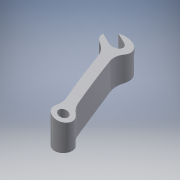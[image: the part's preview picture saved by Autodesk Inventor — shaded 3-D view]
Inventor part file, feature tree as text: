
AUTODESK INVENTOR PART (.ipt)
format: ipt  version: 2016 (Build 200138000, 138)  size: 583,168 bytes
history: native  units: in
note: dims shown in document units (in); Inventor stores cm internally (conversion verified against a paired STEP export)
features: sketch x5, projected_geometry x5, extrude x4, revolve x1, plane x1, pattern_circular x1, fillet x1
ambient origin geometry x8: Origin, YZ Plane, XZ Plane, XY Plane, X Axis, Y Axis, Z Axis, Center Point
bodies: Solid1 (feature_tree)
feature tree (18):
  revolve  "Revolution1"  [1 undecoded]
  plane  "Work Plane1"
  extrude  "Extrusion1"  Depth=0.05in
  pattern_circular  "Circular Pattern1"  [2 undecoded]
  extrude  "Extrusion2"  Depth=0.125in
  extrude  "Extrusion3"  Depth=0.125in
  fillet  "Fillet1"  Radius=0.1in
  extrude  "Extrusion4"  Depth=0.125in TaperAngle=0.0deg
  sketch  "Sketch1"  dims[d0=0.8265in d1=0.175in]
  sketch  "Sketch2"  dims[d2=0.05in d3=0.1in]
  sketch  "Sketch3"  dims[d4=0.15in]
  projected_geometry  "Projected Loop1"
  projected_geometry  "Projected Loop2"
  sketch  "Sketch4"  dims[d5=0.275in]
  projected_geometry  "Projected Loop3"
  projected_geometry  "Projected Loop4"
  sketch  "Sketch5"  dims[d6=90.0deg d7=0.1in d8=0.35in d9=0.2in d10=0.1in d11=1.0in d12=0.0in d13=4.7244in d14=360.0deg d16=0.075in d17=1.0in d18=0.0in d19=0.1in d20=0.025in d22=0.15in d23=0.25in d24=0.14in d25=135.0deg d26=0.05in d27=0.025in d28=0.5in d29=0.2in d30=0.065in d31=1.0in d32=0.0in d33=0.125in d37=0.0197in d38=0.0in]
  projected_geometry  "Projected Loop5"
note: 3 required parameter values undecoded (feature->parameter linkage not recoverable at this tier; creation-order binding heuristic only, values carry confidence <= 0.55)